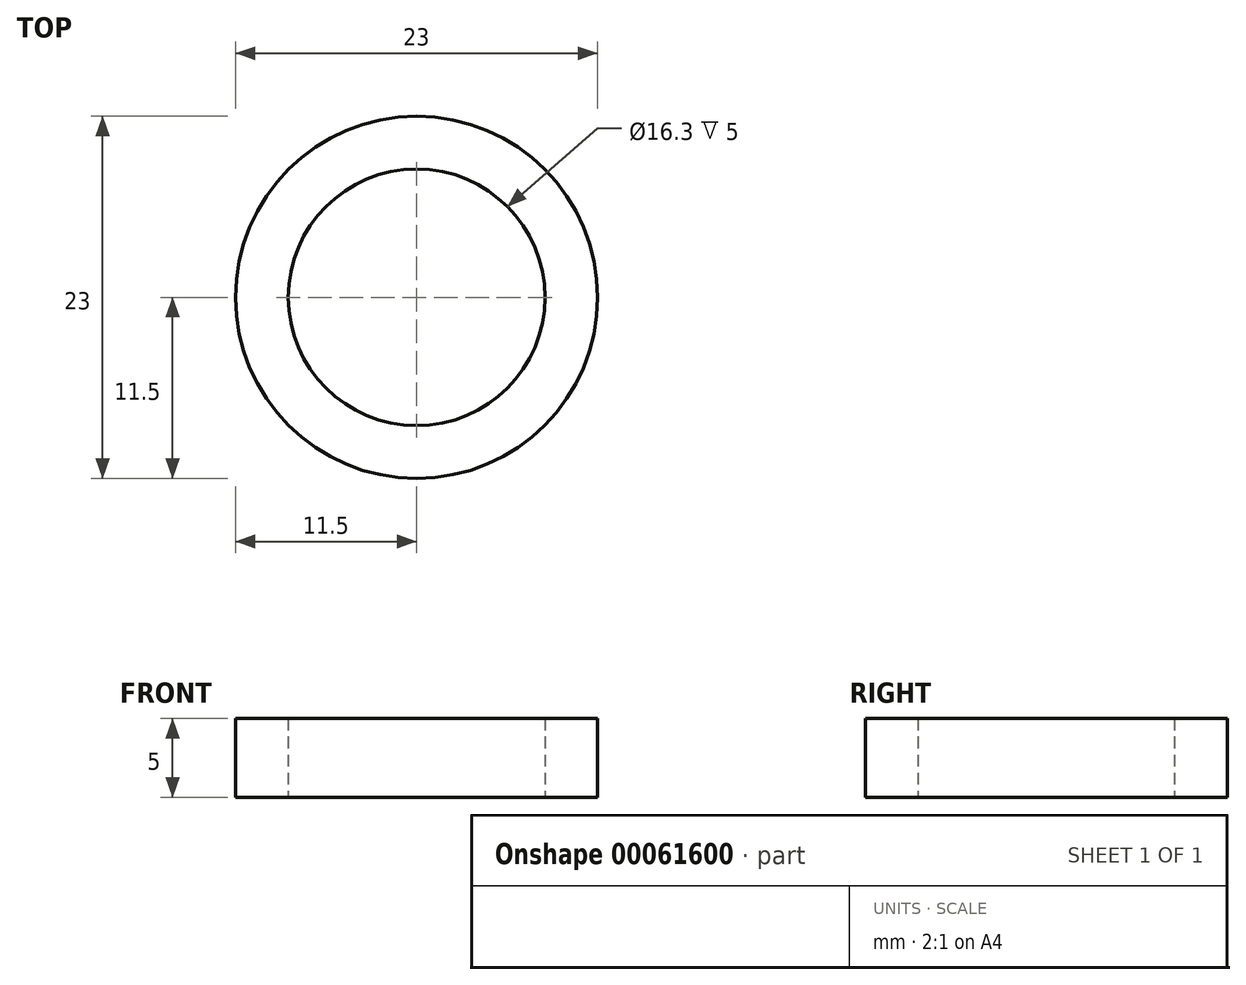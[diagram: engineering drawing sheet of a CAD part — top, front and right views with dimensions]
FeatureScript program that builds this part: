
annotation { "Feature Type Name" : "Feature", "Feature Type Description" : "" }
export const myFeature = defineFeature(function(context is Context, id is Id, definition is map)
    precondition{}
    {
        {
            var Q0;
            Q0=qCreatedBy(makeId("Top.planeOp"),FACE);
            var sketch = newSketch(context, id + "F0", { "sketchPlane" : qUnion([Q0])});
            skCircle(sketch, "E0", {"center": v(0, 0) * mm, "radius": 11.5 * mm});
            skCircle(sketch, "E1", {"center": v(0, 0) * mm, "radius": 8.15 * mm});
            skSolve(sketch);
        }
        {
            var Q0;
            Q0 = qSketchRegion(id + "F0", true);
            extrude(context, id + "F1", {"entities" : qUnion([Q0]), "endBound" : BoundingType.SYMMETRIC, "depth" : 5 * mm});
        }
    });
